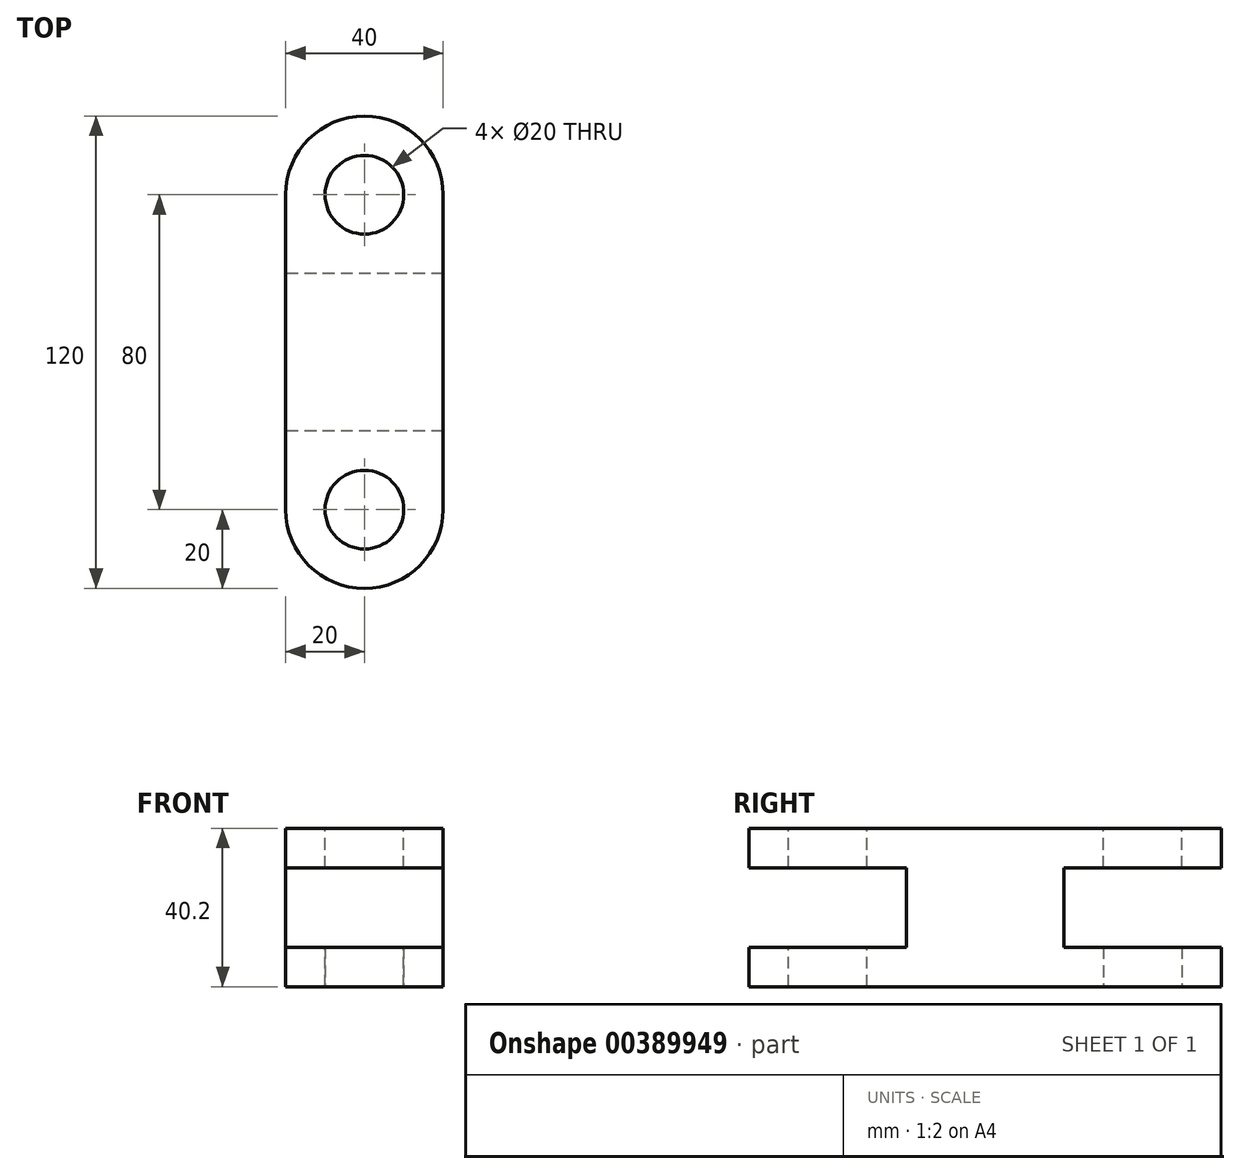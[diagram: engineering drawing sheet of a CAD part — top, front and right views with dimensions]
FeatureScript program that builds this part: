
annotation { "Feature Type Name" : "Feature", "Feature Type Description" : "" }
export const myFeature = defineFeature(function(context is Context, id is Id, definition is map)
    precondition{}
    {
        {
            var Q0;
            Q0=qCreatedBy(makeId("Top.planeOp"),FACE);
            var sketch = newSketch(context, id + "F0", { "sketchPlane" : qUnion([Q0])});
            skLineSegment(sketch, "E0.bottom", {"start": v(20, -40) * mm, "end": v(-20, -40) * mm});
            skLineSegment(sketch, "E0.top", {"start": v(20, 40) * mm, "end": v(-20, 40) * mm});
            skLineSegment(sketch, "E0.left", {"start": v(20, -40) * mm, "end": v(20, 40) * mm});
            skLineSegment(sketch, "E0.right", {"start": v(-20, -40) * mm, "end": v(-20, 40) * mm});
            skPoint(sketch, "E0.middle", {"position": v(0, 0) * mm});
            skSolve(sketch);
        }
        {
            var Q0;
            Q0 = qSketchRegion(id + "F0", true);
            extrude(context, id + "F1", {"entities" : qUnion([Q0]), "depth" : 20.1 * mm});
        }
        {
            var Q0;
            Q0=makeQuery(id+"F1.opExtrude","CAP_FACE",FACE,{"disambiguationData":[OSD([sQuery(id+"F0.wireOp",EDGE,"E0.bottom"),sQuery(id+"F0.wireOp",EDGE,"E0.top"),sQuery(id+"F0.wireOp",EDGE,"E0.left"),sQuery(id+"F0.wireOp",EDGE,"E0.right")])],"isStart":false});
            var sketch = newSketch(context, id + "F2", { "sketchPlane" : qUnion([Q0])});
            skLineSegment(sketch, "E1.bottom", {"start": v(-20, 40) * mm, "end": v(20, 40) * mm});
            skLineSegment(sketch, "E1.left", {"start": v(-20, 40) * mm, "end": v(-20, 60) * mm});
            skLineSegment(sketch, "E1.right", {"start": v(20, 40) * mm, "end": v(20, 60) * mm});
            skArc(sketch, "E2", {"start": v(20, 60) * mm, "mid": v(0, 80) * mm, "end": v(-20, 60) * mm});
            skCircle(sketch, "E3", {"center": v(0, 60) * mm, "radius": 10 * mm});
            skSolve(sketch);
        }
        {
            var Q0;
            Q0 = qSketchRegion(id + "F2", true);
            extrude(context, id + "F3", {"entities" : qUnion([Q0]), "operationType" : NewBodyOperationType.ADD, "oppositeDirection" : true, "depth" : 10 * mm});
        }
        {
            var Q0;
            Q0=makeQuery(id+"F1.opExtrude","SWEPT_BODY",BODY,{"disambiguationData":[OSD([sQuery(id+"F0.wireOp",EDGE,"E0.bottom"),sQuery(id+"F0.wireOp",EDGE,"E0.top"),sQuery(id+"F0.wireOp",EDGE,"E0.left"),sQuery(id+"F0.wireOp",EDGE,"E0.right")])]});
            var Q1;
            Q1=qCreatedBy(makeId("Top.planeOp"),FACE);
            mirror(context, id + "F4", {"operationType" : NewBodyOperationType.ADD, "entities" : qUnion([Q0]), "mirrorPlane" : qUnion([Q1])});
        }
        {
            var Q0;
            Q0=qCreatedBy(makeId("Right.planeOp"),FACE);
            var sketch = newSketch(context, id + "F5", { "sketchPlane" : qUnion([Q0])});
            skLineSegment(sketch, "E4.bottom", {"start": v(0, 10.1) * mm, "end": v(-40, 10.1) * mm});
            skLineSegment(sketch, "E4.top", {"start": v(0, -10.1) * mm, "end": v(-40, -10.1) * mm});
            skLineSegment(sketch, "E4.left", {"start": v(0, 10.1) * mm, "end": v(0, -10.1) * mm});
            skLineSegment(sketch, "E4.right", {"start": v(-40, 10.1) * mm, "end": v(-40, -10.1) * mm});
            skSolve(sketch);
        }
        {
            var Q0;
            Q0 = qSketchRegion(id + "F5", true);
            var Q1;
            {var subQ0=makeQuery(id+"F3.boolean.opBoolean","MERGE",FACE,{"derivedFrom":[makeQuery(id+"F1.opExtrude","SWEPT_FACE",FACE,{"disambiguationData":[OSD([sQuery(id+"F0.wireOp",EDGE,"E0.left")])]}),makeQuery(id+"F3.opExtrude","SWEPT_FACE",FACE,{"disambiguationData":[OSD([sQuery(id+"F2.wireOp",EDGE,"E1.right")])]})]});Q1=makeQuery(id+"F4.boolean.opBoolean","MERGE",FACE,{"derivedFrom":[subQ0,makeQuery(id+"F4.opPattern","COPY",FACE,{"derivedFrom":subQ0,"instanceName":"1"})]});}
            extrude(context, id + "F6", {"entities" : qUnion([Q0]), "operationType" : NewBodyOperationType.REMOVE, "endBound" : BoundingType.SYMMETRIC, "endBoundEntityFace" : qUnion([Q1]), "depth" : 40 * mm});
        }
        {
            var Q0;
            Q0=qCreatedBy(makeId("Top.planeOp"),FACE);
            var sketch = newSketch(context, id + "F7", { "sketchPlane" : qUnion([Q0])});
            skLineSegment(sketch, "E5", {"start": v(0, -20) * mm, "end": v(0, -40) * mm, "construction": true});
            skCircle(sketch, "E6", {"center": v(0, -20) * mm, "radius": 10 * mm});
            skSolve(sketch);
        }
        {
            var Q0;
            Q0 = qSketchRegion(id + "F7", true);
            extrude(context, id + "F8", {"entities" : qUnion([Q0]), "operationType" : NewBodyOperationType.REMOVE, "endBound" : BoundingType.SYMMETRIC, "oppositeDirection" : true, "depth" : 50 * mm});
        }
        {
            var Q0;
            {var subQ2=sQuery(id+"F0.wireOp",EDGE,"E0.left");var subQ4=sQuery(id+"F0.wireOp",EDGE,"E0.bottom");var subQ6=makeQuery(id+"F1.opExtrude","SWEPT_EDGE",EDGE,{"disambiguationData":[OSD([subQ4,subQ2])]});Q0=makeQuery(id+"F6.boolean.opBoolean","SPLIT",EDGE,{"disambiguationData":[TD([makeQuery(id+"F6.opExtrude","SWEPT_FACE",FACE,{"disambiguationData":[OSD([sQuery(id+"F5.wireOp",EDGE,"E4.top")])]})])],"derivedFrom":makeQuery(id+"F4.boolean.opBoolean","MERGE",EDGE,{"derivedFrom":[subQ6,makeQuery(id+"F4.opPattern","COPY",EDGE,{"derivedFrom":subQ6,"instanceName":"1"})]})});}
            var Q1;
            {var subQ2=sQuery(id+"F0.wireOp",EDGE,"E0.bottom");var subQ4=sQuery(id+"F0.wireOp",EDGE,"E0.right");var subQ6=makeQuery(id+"F1.opExtrude","SWEPT_EDGE",EDGE,{"disambiguationData":[OSD([subQ2,subQ4])]});Q1=makeQuery(id+"F6.boolean.opBoolean","SPLIT",EDGE,{"disambiguationData":[TD([makeQuery(id+"F6.opExtrude","SWEPT_FACE",FACE,{"disambiguationData":[OSD([sQuery(id+"F5.wireOp",EDGE,"E4.top")])]})])],"derivedFrom":makeQuery(id+"F4.boolean.opBoolean","MERGE",EDGE,{"derivedFrom":[subQ6,makeQuery(id+"F4.opPattern","COPY",EDGE,{"derivedFrom":subQ6,"instanceName":"1"})]})});}
            var Q2;
            {var subQ1=sQuery(id+"F0.wireOp",EDGE,"E0.right");var subQ2=sQuery(id+"F0.wireOp",EDGE,"E0.bottom");var subQ6=makeQuery(id+"F1.opExtrude","SWEPT_EDGE",EDGE,{"disambiguationData":[OSD([subQ2,subQ1])]});Q2=makeQuery(id+"F6.boolean.opBoolean","SPLIT",EDGE,{"disambiguationData":[TD([makeQuery(id+"F6.opExtrude","SWEPT_FACE",FACE,{"disambiguationData":[OSD([sQuery(id+"F5.wireOp",EDGE,"E4.bottom")])]})])],"derivedFrom":makeQuery(id+"F4.boolean.opBoolean","MERGE",EDGE,{"derivedFrom":[subQ6,makeQuery(id+"F4.opPattern","COPY",EDGE,{"derivedFrom":subQ6,"instanceName":"1"})]})});}
            var Q3;
            {var subQ1=sQuery(id+"F0.wireOp",EDGE,"E0.left");var subQ2=sQuery(id+"F0.wireOp",EDGE,"E0.bottom");var subQ6=makeQuery(id+"F1.opExtrude","SWEPT_EDGE",EDGE,{"disambiguationData":[OSD([subQ2,subQ1])]});Q3=makeQuery(id+"F6.boolean.opBoolean","SPLIT",EDGE,{"disambiguationData":[TD([makeQuery(id+"F6.opExtrude","SWEPT_FACE",FACE,{"disambiguationData":[OSD([sQuery(id+"F5.wireOp",EDGE,"E4.bottom")])]})])],"derivedFrom":makeQuery(id+"F4.boolean.opBoolean","MERGE",EDGE,{"derivedFrom":[subQ6,makeQuery(id+"F4.opPattern","COPY",EDGE,{"derivedFrom":subQ6,"instanceName":"1"})]})});}
            fillet(context, id + "F9", {"entities" : qUnion([Q0, Q1, Q2, Q3]), "radius" : 20 * mm, "tangentPropagation" : true, "allowEdgeOverflow" : false});
        }
    });
